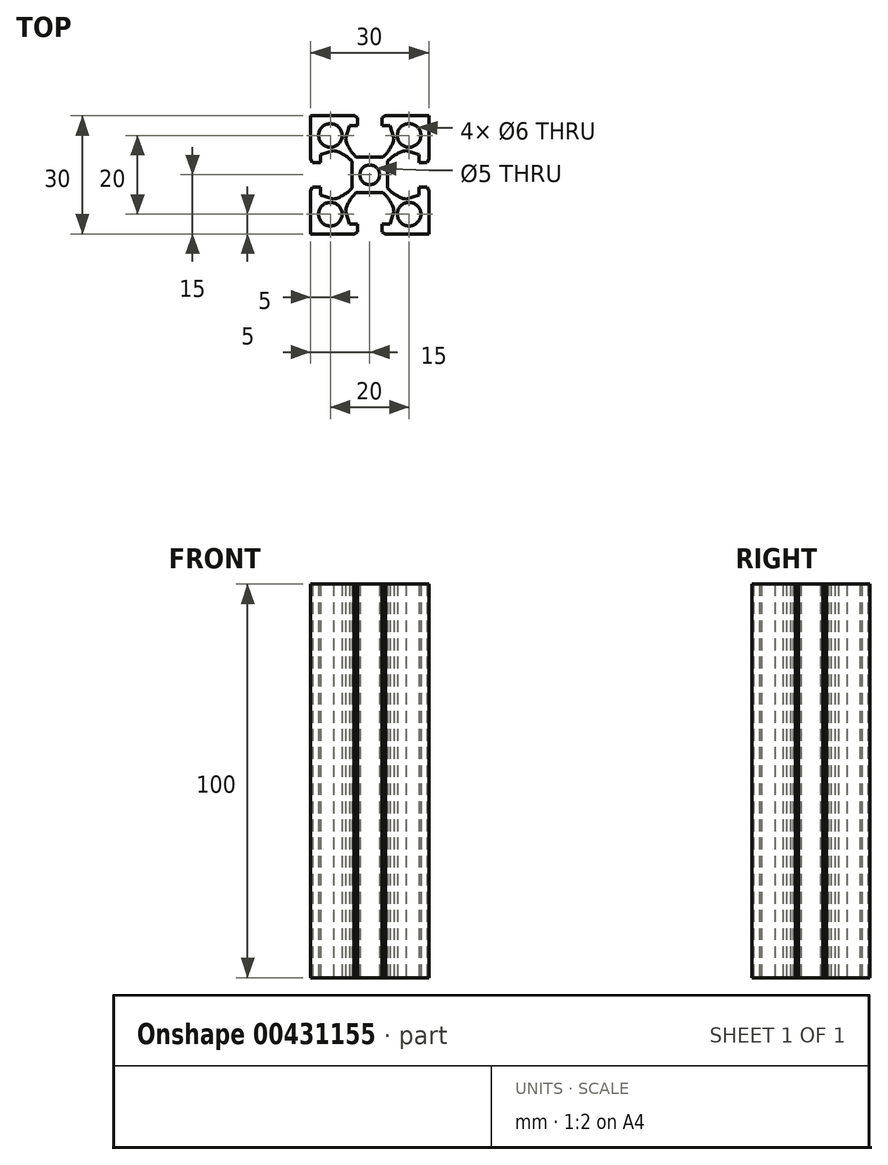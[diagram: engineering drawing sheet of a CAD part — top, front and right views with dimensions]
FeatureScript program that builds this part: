
annotation { "Feature Type Name" : "Feature", "Feature Type Description" : "" }
export const myFeature = defineFeature(function(context is Context, id is Id, definition is map)
    precondition{}
    {
        {
            var Q0;
            Q0=qCreatedBy(makeId("Top.planeOp"),FACE);
            var sketch = newSketch(context, id + "F0", { "sketchPlane" : qUnion([Q0])});
            skLineSegment(sketch, "E0.bottom", {"start": v(15, 15) * mm, "end": v(3.95, 15) * mm});
            skLineSegment(sketch, "E0.top", {"start": v(15, -15) * mm, "end": v(3.95, -15) * mm});
            skLineSegment(sketch, "E0.left", {"start": v(15, 15) * mm, "end": v(15, 3.95) * mm});
            skLineSegment(sketch, "E0.right", {"start": v(-15, 15) * mm, "end": v(-15, 3.95) * mm});
            skPoint(sketch, "E0.middle", {"position": v(0, 0) * mm});
            skLineSegment(sketch, "E1", {"start": v(0, 15) * mm, "end": v(0, -15) * mm, "construction": true});
            skLineSegment(sketch, "E2", {"start": v(-15, 0) * mm, "end": v(15, 0) * mm, "construction": true});
            skCircle(sketch, "E3", {"center": v(-10, 10) * mm, "radius": 3 * mm});
            skCircle(sketch, "E4", {"center": v(0, 0) * mm, "radius": 2.5 * mm});
            skLineSegment(sketch, "E5", {"start": v(0, 15) * mm, "end": v(0, 12.5) * mm, "construction": true});
            skLineSegment(sketch, "E6", {"start": v(-3.15, 14.5) * mm, "end": v(-3.15, 12.5) * mm});
            skLineSegment(sketch, "E7", {"start": v(-3.15, 12.5) * mm, "end": v(-5.1, 12.5) * mm});
            skLineSegment(sketch, "E8", {"start": v(0, 0) * mm, "end": v(-3.44, 0) * mm, "construction": true});
            skLineSegment(sketch, "E9", {"start": v(-5.1, 12.5) * mm, "end": v(-6.18, 9.16) * mm});
            skLineSegment(sketch, "E10", {"start": v(-3.44, 4.5) * mm, "end": v(0, 4.5) * mm});
            skLineSegment(sketch, "E11", {"start": v(3.36, 15) * mm, "end": v(3.36, 11.64) * mm, "construction": true});
            skArc(sketch, "E12", {"start": v(-3.44, 4.5) * mm, "mid": v(-5.13, 6.64) * mm, "end": v(-6.18, 9.16) * mm});
            skLineSegment(sketch, "E13", {"start": v(-3.95, 15) * mm, "end": v(-3.15, 14.5) * mm});
            skLineSegment(sketch, "E14.trimOffspring", {"start": v(-3.95, 15) * mm, "end": v(-5.1, 15) * mm, "construction": true});
            skLineSegment(sketch, "E15", {"start": v(-15, 15) * mm, "end": v(15, -15) * mm, "construction": true});
            skLineSegment(sketch, "E16", {"start": v(15, 15) * mm, "end": v(-15, -15) * mm, "construction": true});
            skArc(sketch, "E17.MirrorCS", {"start": v(-4.5, 3.43) * mm, "mid": v(-6.64, 5.13) * mm, "end": v(-9.16, 6.18) * mm});
            skLineSegment(sketch, "E18.MirrorCS", {"start": v(-4.5, 3.43) * mm, "end": v(-4.5, 0) * mm});
            skLineSegment(sketch, "E19.MirrorCS", {"start": v(-12.5, 5.1) * mm, "end": v(-9.16, 6.18) * mm});
            skLineSegment(sketch, "E20.MirrorCS", {"start": v(-12.5, 3.15) * mm, "end": v(-12.5, 5.1) * mm});
            skLineSegment(sketch, "E21.MirrorCS", {"start": v(-15, 3.95) * mm, "end": v(-14.5, 3.15) * mm});
            skLineSegment(sketch, "E22.MirrorCS", {"start": v(-14.5, 3.15) * mm, "end": v(-12.5, 3.15) * mm});
            skLineSegment(sketch, "E23.MirrorCS", {"start": v(-14.5, -3.15) * mm, "end": v(-12.5, -3.15) * mm});
            skLineSegment(sketch, "E24.MirrorCS", {"start": v(-15, -3.95) * mm, "end": v(-14.5, -3.15) * mm});
            skLineSegment(sketch, "E25.MirrorCS", {"start": v(-12.5, -3.15) * mm, "end": v(-12.5, -5.1) * mm});
            skLineSegment(sketch, "E26.MirrorCS", {"start": v(-12.5, -5.1) * mm, "end": v(-9.16, -6.18) * mm});
            skArc(sketch, "E27.MirrorCS", {"start": v(-4.5, -3.43) * mm, "mid": v(-6.64, -5.13) * mm, "end": v(-9.16, -6.18) * mm});
            skLineSegment(sketch, "E28.MirrorCS", {"start": v(-4.5, -3.43) * mm, "end": v(-4.5, 0) * mm});
            skLineSegment(sketch, "E29.MirrorCS", {"start": v(-3.44, -4.5) * mm, "end": v(0, -4.5) * mm});
            skArc(sketch, "E30.MirrorCS", {"start": v(-3.44, -4.5) * mm, "mid": v(-5.13, -6.64) * mm, "end": v(-6.18, -9.16) * mm});
            skLineSegment(sketch, "E31.MirrorCS", {"start": v(-5.1, -12.5) * mm, "end": v(-6.18, -9.16) * mm});
            skLineSegment(sketch, "E32.MirrorCS", {"start": v(-3.15, -12.5) * mm, "end": v(-5.1, -12.5) * mm});
            skLineSegment(sketch, "E33.MirrorCS", {"start": v(-3.95, -15) * mm, "end": v(-3.15, -14.5) * mm});
            skLineSegment(sketch, "E34.MirrorCS", {"start": v(-3.15, -14.5) * mm, "end": v(-3.15, -12.5) * mm});
            skLineSegment(sketch, "E35.MirrorCS", {"start": v(3.44, -4.5) * mm, "end": v(0, -4.5) * mm});
            skArc(sketch, "E36.MirrorCS", {"start": v(3.44, -4.5) * mm, "mid": v(5.13, -6.64) * mm, "end": v(6.18, -9.16) * mm});
            skLineSegment(sketch, "E37.MirrorCS", {"start": v(5.1, -12.5) * mm, "end": v(6.18, -9.16) * mm});
            skLineSegment(sketch, "E38.MirrorCS", {"start": v(3.15, -12.5) * mm, "end": v(5.1, -12.5) * mm});
            skLineSegment(sketch, "E39.MirrorCS", {"start": v(3.15, -14.5) * mm, "end": v(3.15, -12.5) * mm});
            skLineSegment(sketch, "E40.MirrorCS", {"start": v(3.95, -15) * mm, "end": v(3.15, -14.5) * mm});
            skArc(sketch, "E41.MirrorCS", {"start": v(4.5, -3.43) * mm, "mid": v(6.64, -5.13) * mm, "end": v(9.16, -6.18) * mm});
            skLineSegment(sketch, "E42.MirrorCS", {"start": v(4.5, 3.44) * mm, "end": v(4.5, 0) * mm});
            skLineSegment(sketch, "E43.MirrorCS", {"start": v(4.5, -3.43) * mm, "end": v(4.5, 0) * mm});
            skArc(sketch, "E44.MirrorCS", {"start": v(4.5, 3.44) * mm, "mid": v(6.64, 5.13) * mm, "end": v(9.16, 6.18) * mm});
            skLineSegment(sketch, "E45.MirrorCS", {"start": v(12.5, 5.1) * mm, "end": v(9.16, 6.18) * mm});
            skLineSegment(sketch, "E46.MirrorCS", {"start": v(12.5, -5.1) * mm, "end": v(9.16, -6.18) * mm});
            skLineSegment(sketch, "E47.MirrorCS", {"start": v(12.5, -3.15) * mm, "end": v(12.5, -5.1) * mm});
            skLineSegment(sketch, "E48.MirrorCS", {"start": v(14.5, -3.15) * mm, "end": v(12.5, -3.15) * mm});
            skLineSegment(sketch, "E49.MirrorCS", {"start": v(12.5, 3.15) * mm, "end": v(12.5, 5.1) * mm});
            skLineSegment(sketch, "E50.MirrorCS", {"start": v(14.5, 3.15) * mm, "end": v(12.5, 3.15) * mm});
            skLineSegment(sketch, "E51.MirrorCS", {"start": v(15, 3.95) * mm, "end": v(14.5, 3.15) * mm});
            skLineSegment(sketch, "E52.MirrorCS", {"start": v(15, -3.95) * mm, "end": v(14.5, -3.15) * mm});
            skLineSegment(sketch, "E53.MirrorCS", {"start": v(3.43, 4.5) * mm, "end": v(0, 4.5) * mm});
            skArc(sketch, "E54.MirrorCS", {"start": v(3.43, 4.5) * mm, "mid": v(5.13, 6.64) * mm, "end": v(6.18, 9.16) * mm});
            skLineSegment(sketch, "E55.MirrorCS", {"start": v(5.1, 12.5) * mm, "end": v(6.18, 9.16) * mm});
            skLineSegment(sketch, "E56.MirrorCS", {"start": v(3.15, 12.5) * mm, "end": v(5.1, 12.5) * mm});
            skLineSegment(sketch, "E57.MirrorCS", {"start": v(3.15, 14.5) * mm, "end": v(3.15, 12.5) * mm});
            skLineSegment(sketch, "E58.MirrorCS", {"start": v(3.95, 15) * mm, "end": v(3.15, 14.5) * mm});
            skCircle(sketch, "E59.MirrorC", {"center": v(10, 10) * mm, "radius": 3 * mm});
            skCircle(sketch, "E60.MirrorC", {"center": v(10, -10) * mm, "radius": 3 * mm});
            skCircle(sketch, "E61.MirrorC", {"center": v(-10, -10) * mm, "radius": 3 * mm});
            skLineSegment(sketch, "E62.trimOffspring", {"start": v(-15, -3.95) * mm, "end": v(-15, -15) * mm});
            skPoint(sketch, "E63.orphan", {"position": v(-15, 3.15) * mm});
            skPoint(sketch, "E64.orphan", {"position": v(-15, -3.15) * mm});
            skLineSegment(sketch, "E65.trimOffspring", {"start": v(-3.95, -15) * mm, "end": v(-15, -15) * mm});
            skPoint(sketch, "E66.orphan", {"position": v(-3.15, -15) * mm});
            skPoint(sketch, "E67.orphan", {"position": v(3.15, -15) * mm});
            skLineSegment(sketch, "E68.trimOffspring", {"start": v(15, -3.95) * mm, "end": v(15, -15) * mm});
            skPoint(sketch, "E69.orphan", {"position": v(15, 3.15) * mm});
            skPoint(sketch, "E70.orphan", {"position": v(15, -3.15) * mm});
            skPoint(sketch, "E71.trimOffspring.end.orphan", {"position": v(3.15, 15) * mm});
            skLineSegment(sketch, "E72.trimOffspring", {"start": v(-3.95, 15) * mm, "end": v(-15, 15) * mm});
            skPoint(sketch, "E73.trimOffspring.end.orphan", {"position": v(-3.15, 15) * mm});
            skSolve(sketch);
        }
        {
            var Q0;
            Q0=makeQuery(id+"F0.imprint","IMPRINT",FACE,{"disambiguationData":[TD([[makeQuery(id+"F0.imprint","IMPRINT",EDGE,{"derivedFrom":sQuery(id+"F0.wireOp",EDGE,"E0.bottom")}),1.0]])]});
            extrude(context, id + "F1", {"entities" : qUnion([Q0]), "endBound" : BoundingType.SYMMETRIC, "depth" : 100 * mm});
        }
    });
